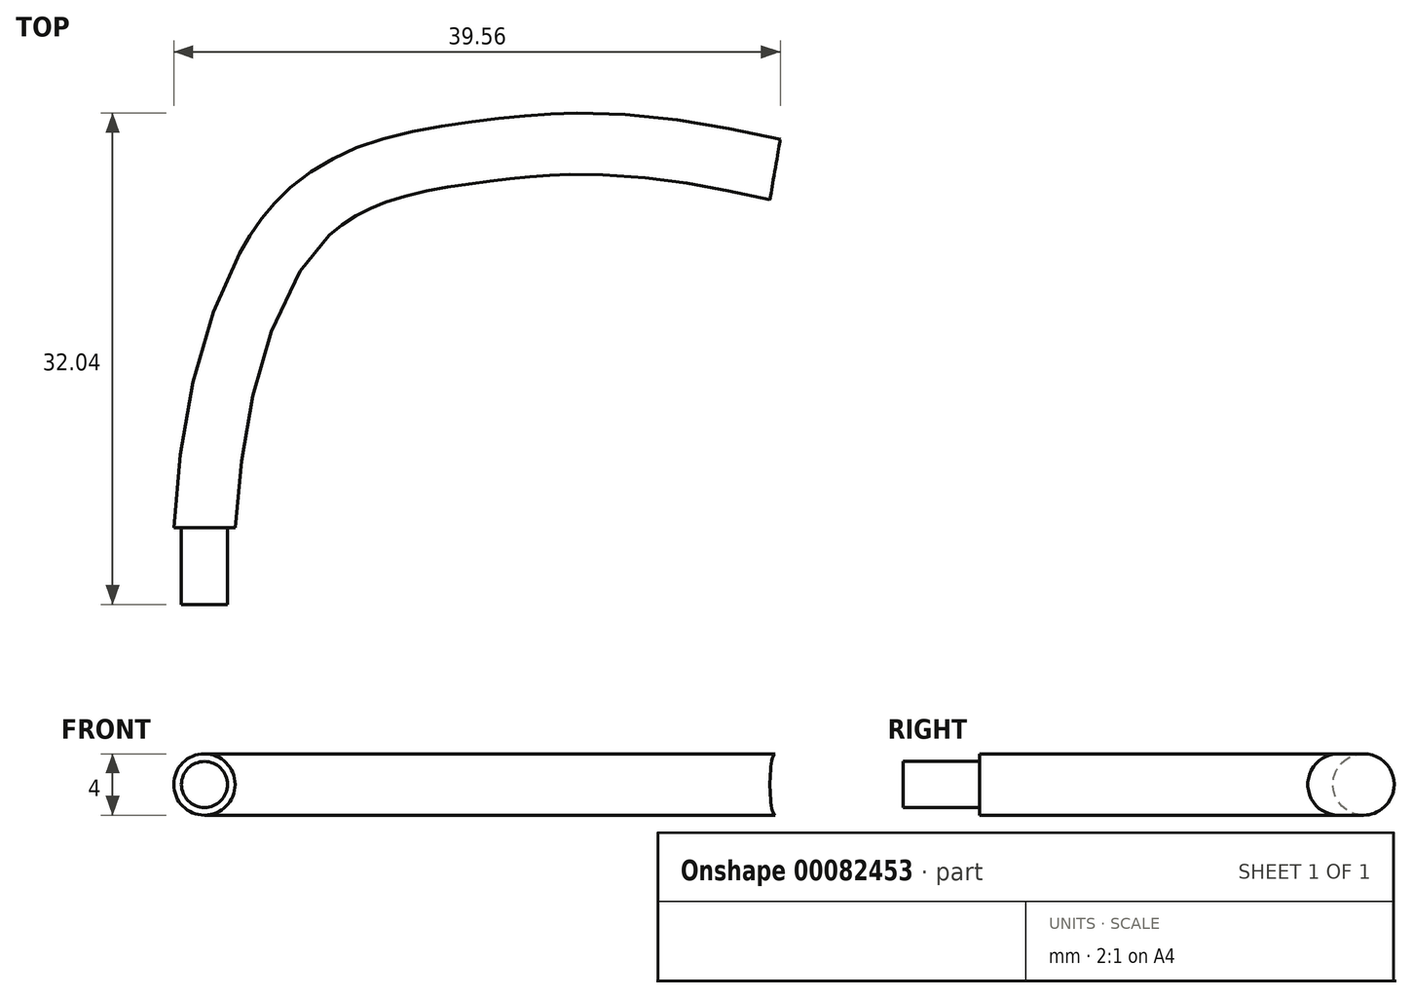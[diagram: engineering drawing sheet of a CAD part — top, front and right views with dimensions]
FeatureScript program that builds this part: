
annotation { "Feature Type Name" : "Feature", "Feature Type Description" : "" }
export const myFeature = defineFeature(function(context is Context, id is Id, definition is map)
    precondition{}
    {
        {
            var Q0;
            Q0=qCreatedBy(makeId("Front.planeOp"),FACE);
            var sketch = newSketch(context, id + "F0", { "sketchPlane" : qUnion([Q0])});
            skArc(sketch, "E0", {"start": v(-30.63, 1.9) * mm, "mid": v(-29.9, -2) * mm, "end": v(-29.58, 1.96) * mm});
            skArc(sketch, "E1", {"start": v(-29.58, 1.96) * mm, "mid": v(-30.1, 2) * mm, "end": v(-30.63, 1.9) * mm});
            skSolve(sketch);
        }
        {
            var Q0;
            Q0=qCreatedBy(makeId("Top.planeOp"),FACE);
            var sketch = newSketch(context, id + "F1", { "sketchPlane" : qUnion([Q0])});
            skFitSpline(sketch, "E2", {"points": [v(-30, 0) * mm, v(-23.58, 20.21) * mm, v(-12.06, 24.53) * mm, v(7.22, 23.38) * mm], "startDerivative": vector(3.63, 64.62) * mm, "endDerivative": vector(81.73, -18.73) * mm});
            skSolve(sketch);
        }
        {
            var Q0;
            Q0=makeQuery(id+"F0.imprint","IMPRINT",FACE,{"disambiguationData":[TD([[makeQuery(id+"F0.imprint","IMPRINT",EDGE,{"derivedFrom":sQuery(id+"F0.wireOp",EDGE,"E0")}),1.0]])]});
            var Q1;
            Q1=sQuery(id+"F0.wireOp",EDGE,"E0");
            var Q2;
            Q2=sQuery(id+"F1.wireOp",EDGE,"E2");
            sweep(context, id + "F2", {"profiles" : qUnion([Q0]), "surfaceProfiles" : qUnion([Q1]), "path" : qUnion([Q2])});
        }
        {
            var Q0;
            Q0=makeQuery(id+"F0.imprint","IMPRINT",FACE,{"disambiguationData":[TD([[makeQuery(id+"F0.imprint","IMPRINT",EDGE,{"derivedFrom":sQuery(id+"F0.wireOp",EDGE,"E0")}),1.0]])]});
            var sketch = newSketch(context, id + "F3", { "sketchPlane" : qUnion([Q0])});
            skCircle(sketch, "E3", {"center": v(-30, 0) * mm, "radius": 1.5 * mm});
            skSolve(sketch);
        }
        {
            var Q0;
            Q0 = qSketchRegion(id + "F3", true);
            extrude(context, id + "F4", {"entities" : qUnion([Q0]), "depth" : 5 * mm});
        }
    });
